# Revit family: Zumtobel MICROS2
name_source: partatom
category: Lighting Fixtures
revit_build: Autodesk Revit 2018 (Build: 20170223_1515(x64)
units: mm (PartAtom-declared; Revit-internal decimal feet)

## family parameters
Cut with Voids When Loaded = No
Host = Face
Light Source = Yes
OmniClass Number = 23.80.70.11
OmniClass Title = Luminaries for Internal Lighting
Part Type = Normal
Room Calculation Point = No
Round Connector Dimension = Use Diameter
Shared = No

## types (4) — shared parameters
Assembly Code = D5020200
Color Filter = 16777215
Dimming Lamp Color Temperature Shift = <None>
Lamp = LED
Manufacturer = Zumtobel Lighting
URL = http://www.zumtobel.com
Voltage = 230 V
zero-valued in all types: Default Elevation

## per-type parameters (varying)
| type | Apparent Load | Description | Height | Length | Model | Offset | Opening Radius | Photometric Web File | R100 | R100 Recessed Body | R100 Surface Mount Body | R68 | R68 Recessed Body | R68 Surface Mount Body | Tilt Angle | Width |
| MICROS2 R100 Recessed | 12 VA | LED ceiling-recessed luminaire | 74 mm | 112 mm | 60300078 | 0 mm  [stored 0 ft] | 50 mm  [stored 0.164042 ft] | 60300078_(STD_LEO).IES | Yes | Yes | No | No | No | No | 35.00° | 112 mm |
| MICROS2 R68 Recessed | 8 VA | LED surface mount luminaire | 120 mm | 83 mm | 60300088 | 0 mm  [stored 0 ft] | 32 mm  [stored 0.104987 ft] | 60300088_(STD_LEO).IES | No | No | No | Yes | Yes | No | 0.00° | 83 mm |
| MICROS2 R100 Surface Mount | 15 VA | LED surface mount luminaire | 140 mm  [stored 0.459318 ft] | 115 mm | 60819444 | 140 mm  [stored 0.459318 ft] | 32 mm  [stored 0.104987 ft] | 60819444_(STD_LEO).IES | Yes | No | Yes | No | No | No | 35.00° | 115 mm |
| MICROS2 R68 Surface Mount | 8 VA | LED surface mount luminaire | 120 mm | 83 mm | 60819294 | 120 mm | 32 mm  [stored 0.104987 ft] | 60819294_(STD_LEO).IES | No | No | No | Yes | No | Yes | 35.00° | 83 mm |

note: [stored X ft] marks values corroborated as IEEE doubles in the binary element streams (Revit-internal decimal feet)

## geometry (parser evidence)
native form markers: Sweep x5
no freeform markers — native parametric forms only
